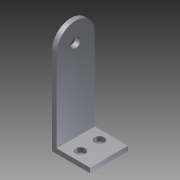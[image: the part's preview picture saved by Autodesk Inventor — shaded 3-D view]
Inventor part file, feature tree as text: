
AUTODESK INVENTOR PART (.ipt)
format: ipt  version: 2012 (Build 160160000, 160)  size: 105,472 bytes
history: native  units: in
note: dims shown in document units (in); Inventor stores cm internally (conversion verified against a paired STEP export)
features: extrude x3, sketch x3
ambient origin geometry x8: Origin, YZ Plane, XZ Plane, XY Plane, X Axis, Y Axis, Z Axis, Center Point
bodies: Solid1 (feature_tree)
feature tree (6):
  extrude  "Extrusion1"  Depth=0.125in
  extrude  "Extrusion2"  Depth=1.0in
  extrude  "Extrusion3"  Depth=0.5in
  sketch  "Sketch1"  dims[d0=0.125in d1=0.125in]
  sketch  "Sketch2"  dims[d2=3.0in d3=1.0in]
  sketch  "Sketch3"  dims[d4=1.0in d5=0.0in d6=0.5in d7=0.25in d8=0.25in d9=0.25in d10=0.25in d11=0.5in d12=1.0in d13=0.0in d14=0.25in d15=2.28in d16=0.5in d17=1.0in d18=0.0in]
